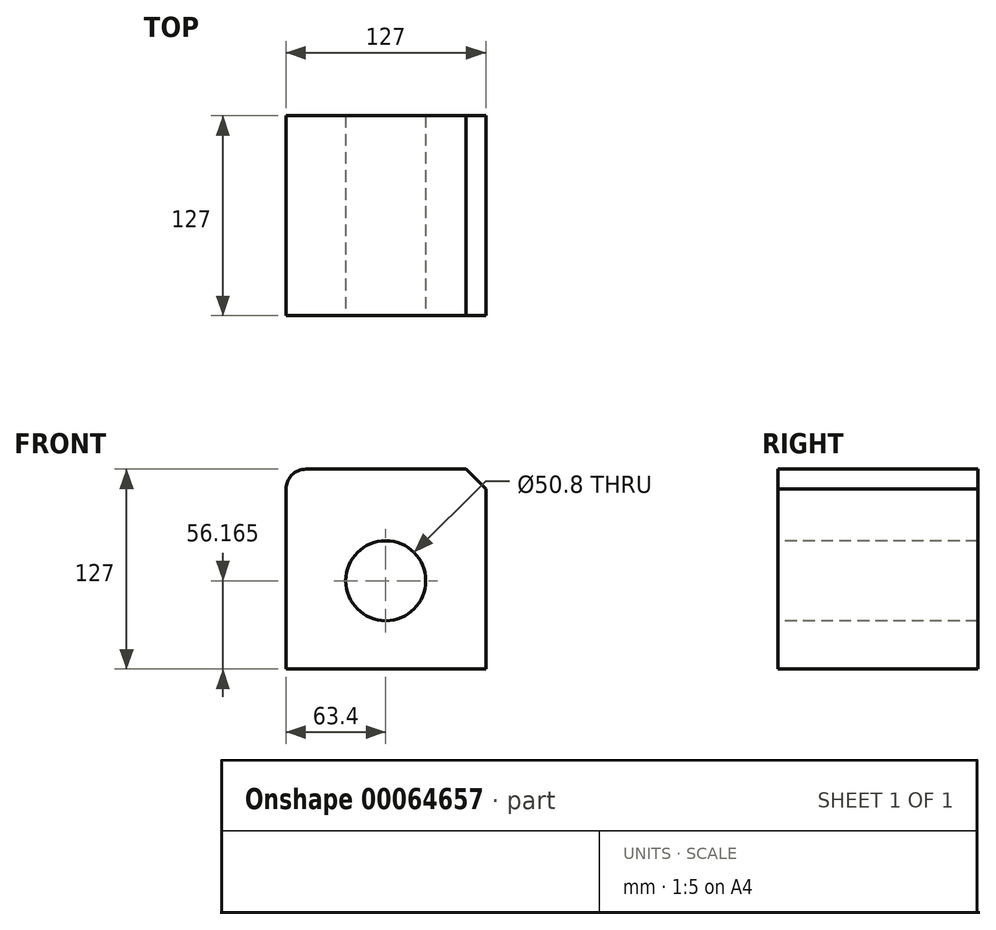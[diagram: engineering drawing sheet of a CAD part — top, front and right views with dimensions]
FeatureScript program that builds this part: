
annotation { "Feature Type Name" : "Feature", "Feature Type Description" : "" }
export const myFeature = defineFeature(function(context is Context, id is Id, definition is map)
    precondition{}
    {
        {
            var Q0;
            Q0=qCreatedBy(makeId("Front.planeOp"),FACE);
            var sketch = newSketch(context, id + "F0", { "sketchPlane" : qUnion([Q0])});
            skLineSegment(sketch, "E0.bottom", {"start": v(-63.4, 127) * mm, "end": v(63.6, 127) * mm});
            skLineSegment(sketch, "E0.top", {"start": v(-63.4, 0) * mm, "end": v(63.6, 0) * mm});
            skLineSegment(sketch, "E0.left", {"start": v(-63.4, 127) * mm, "end": v(-63.4, 0) * mm});
            skLineSegment(sketch, "E0.right", {"start": v(63.6, 127) * mm, "end": v(63.6, 0) * mm});
            skSolve(sketch);
        }
        {
            var Q0;
            Q0=makeQuery(id+"F0.imprint","IMPRINT",FACE,{"disambiguationData":[TD([[makeQuery(id+"F0.imprint","IMPRINT",EDGE,{"derivedFrom":sQuery(id+"F0.wireOp",EDGE,"E0.bottom")}),-1.0]])]});
            extrude(context, id + "F1", {"entities" : qUnion([Q0]), "depth" : 127 * mm});
        }
        {
            var Q0;
            Q0=makeQuery(id+"F1.opExtrude","SWEPT_EDGE",EDGE,{"disambiguationData":[OSD([sQuery(id+"F0.wireOp",EDGE,"E0.bottom"),sQuery(id+"F0.wireOp",EDGE,"E0.left")])]});
            fillet(context, id + "F2", {"entities" : qUnion([Q0]), "radius" : 12.7 * mm, "tangentPropagation" : true, "allowEdgeOverflow" : false});
        }
        {
            var Q0;
            Q0=makeQuery(id+"F1.opExtrude","SWEPT_EDGE",EDGE,{"disambiguationData":[OSD([sQuery(id+"F0.wireOp",EDGE,"E0.bottom"),sQuery(id+"F0.wireOp",EDGE,"E0.right")])]});
            chamfer(context, id + "F3", {"entities" : qUnion([Q0]), "width" : 12.7 * mm, "tangentPropagation" : true});
        }
        {
            var Q0;
            Q0=makeQuery(id+"F1.opExtrude","CAP_FACE",FACE,{"disambiguationData":[OSD([sQuery(id+"F0.wireOp",EDGE,"E0.bottom"),sQuery(id+"F0.wireOp",EDGE,"E0.top"),sQuery(id+"F0.wireOp",EDGE,"E0.left"),sQuery(id+"F0.wireOp",EDGE,"E0.right")])],"isStart":false});
            var sketch = newSketch(context, id + "F4", { "sketchPlane" : qUnion([Q0])});
            skSolve(sketch);
        }
        {
            var Q0;
            {var subQ2=sQuery(id+"F0.wireOp",EDGE,"E0.top");Q0=makeQuery(id+"F4.imprint","IMPRINT",FACE,{"disambiguationData":[TD([[makeQuery(id+"F4.imprint","IMPRINT",EDGE,{"derivedFrom":makeQuery(id+"F1.opExtrude","CAP_EDGE",EDGE,{"disambiguationData":[OSD([subQ2])],"isStart":false})}),1.0]])]});}
            var sketch = newSketch(context, id + "F5", { "sketchPlane" : qUnion([Q0])});
            skCircle(sketch, "E1", {"center": v(0, 56.17) * mm, "radius": 25.4 * mm});
            skSolve(sketch);
        }
        {
            var Q0;
            Q0=makeQuery(id+"F5.imprint","IMPRINT",FACE,{"disambiguationData":[TD([[makeQuery(id+"F5.imprint","IMPRINT",EDGE,{"derivedFrom":sQuery(id+"F5.wireOp",EDGE,"E1")}),1.0]])]});
            extrude(context, id + "F6", {"entities" : qUnion([Q0]), "operationType" : NewBodyOperationType.REMOVE, "endBound" : BoundingType.THROUGH_ALL, "oppositeDirection" : true, "depth" : 25.4 * mm});
        }
    });
